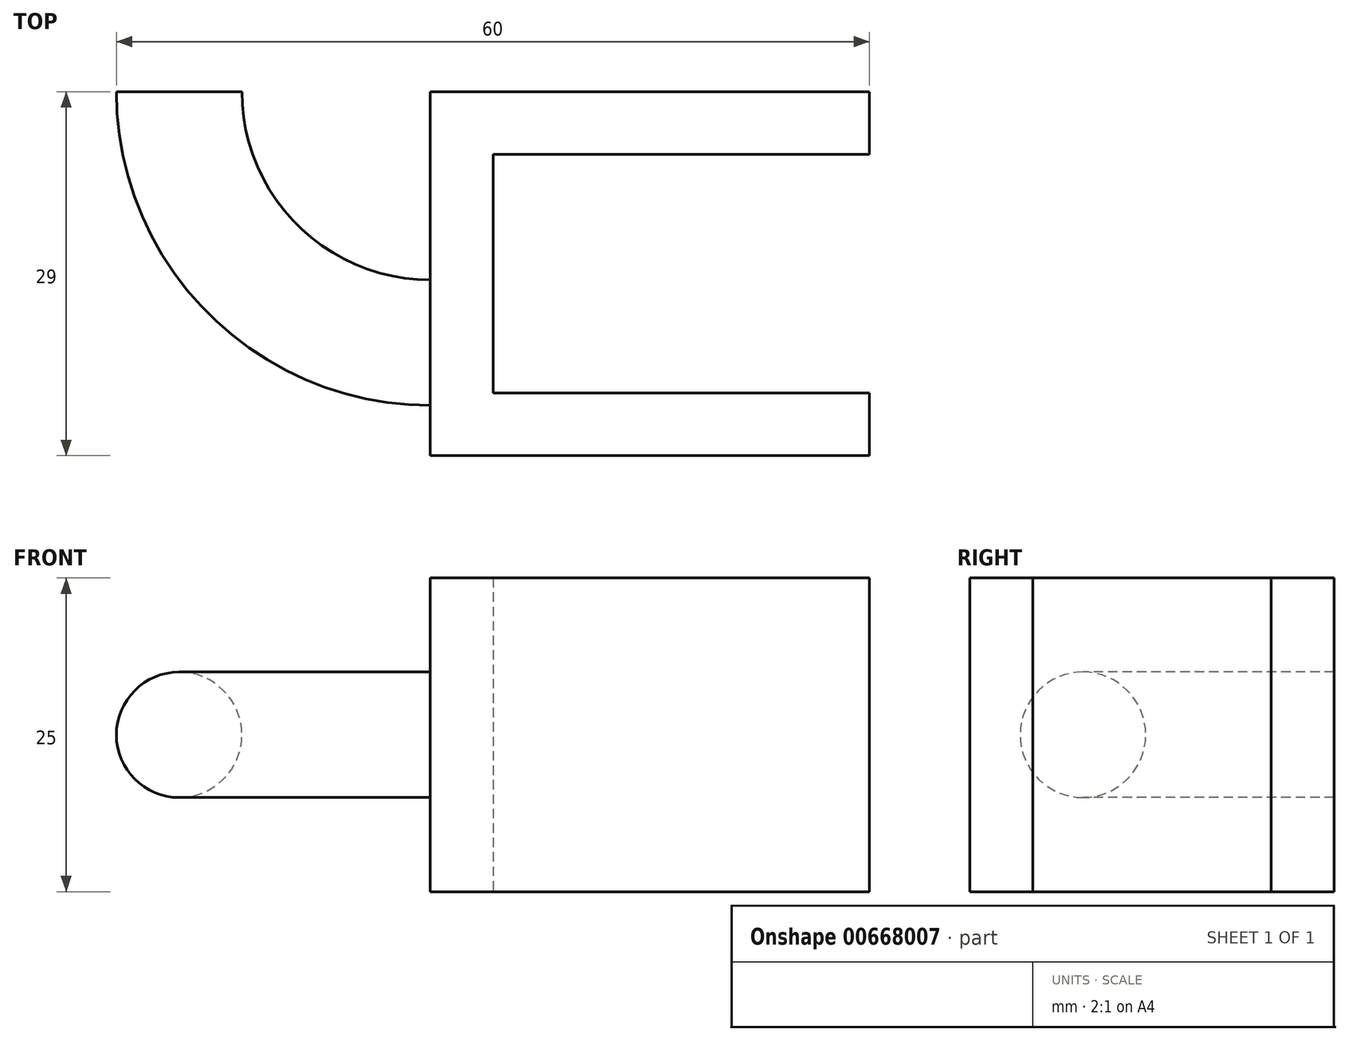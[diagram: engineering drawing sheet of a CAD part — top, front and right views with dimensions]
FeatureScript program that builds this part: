
annotation { "Feature Type Name" : "Feature", "Feature Type Description" : "" }
export const myFeature = defineFeature(function(context is Context, id is Id, definition is map)
    precondition{}
    {
        {
            var Q0;
            Q0=qCreatedBy(makeId("Top.planeOp"),FACE);
            var sketch = newSketch(context, id + "F0", { "sketchPlane" : qUnion([Q0])});
            skLineSegment(sketch, "E0.bottom", {"start": v(-18.33, 11.25) * mm, "end": v(16.67, 11.25) * mm});
            skLineSegment(sketch, "E0.top", {"start": v(-18.33, -17.75) * mm, "end": v(16.67, -17.75) * mm});
            skLineSegment(sketch, "E0.left", {"start": v(-18.33, 11.25) * mm, "end": v(-18.33, -17.75) * mm});
            skLineSegment(sketch, "E0.right", {"start": v(16.67, 11.25) * mm, "end": v(16.67, 6.25) * mm});
            skLineSegment(sketch, "E1.bottom", {"start": v(16.67, 6.25) * mm, "end": v(-13.33, 6.25) * mm});
            skLineSegment(sketch, "E1.top", {"start": v(16.67, -12.75) * mm, "end": v(-13.33, -12.75) * mm});
            skLineSegment(sketch, "E1.right", {"start": v(-13.33, 6.25) * mm, "end": v(-13.33, -12.75) * mm});
            skLineSegment(sketch, "E2.trimOffspring", {"start": v(16.67, -12.75) * mm, "end": v(16.67, -17.75) * mm});
            skSolve(sketch);
        }
        {
            var Q0;
            Q0=makeQuery(id+"F0.imprint","IMPRINT",FACE,{"disambiguationData":[TD([[makeQuery(id+"F0.imprint","IMPRINT",EDGE,{"derivedFrom":sQuery(id+"F0.wireOp",EDGE,"E0.bottom")}),-1.0]])]});
            extrude(context, id + "F1", {"entities" : qUnion([Q0]), "depth" : 25 * mm, "offsetDistance" : 25 * mm});
        }
        {
            var Q0;
            Q0=makeQuery(id+"F1.opExtrude","SWEPT_FACE",FACE,{"disambiguationData":[OSD([sQuery(id+"F0.wireOp",EDGE,"E0.left")])]});
            var sketch = newSketch(context, id + "F2", { "sketchPlane" : qUnion([Q0])});
            skCircle(sketch, "E3", {"center": v(8.75, 12.5) * mm, "radius": 5 * mm});
            skLineSegment(sketch, "E4", {"start": v(-11.25, -9.82) * mm, "end": v(-11.25, 37.57) * mm, "construction": true});
            skSolve(sketch);
        }
        {
            var Q0;
            Q0=makeQuery(id+"F2.imprint","IMPRINT",FACE,{"disambiguationData":[TD([[makeQuery(id+"F2.imprint","IMPRINT",EDGE,{"derivedFrom":sQuery(id+"F2.wireOp",EDGE,"E3")}),1.0]])]});
            var Q1;
            Q1=sQuery(id+"F2.wireOp",EDGE,"E4");
            revolve(context, id + "F3", {"operationType" : NewBodyOperationType.ADD, "entities" : qUnion([Q0]), "axis" : qUnion([Q1]), "revolveType" : RevolveType.ONE_DIRECTION, "oppositeDirection" : true, "angle" : 90 * degree});
        }
    });
